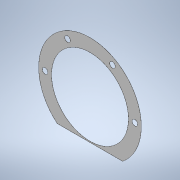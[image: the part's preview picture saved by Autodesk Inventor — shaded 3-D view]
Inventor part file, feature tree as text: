
AUTODESK INVENTOR PART (.ipt)
format: ipt  version: 2020 (Build 240168000, 168)  size: 114,176 bytes
history: native  units: mm
features: other x3, plane x1, extrude x1, sketch x1, reference x1
ambient origin geometry x8: Origin, YZ Plane, XZ Plane, XY Plane, X Axis, Y Axis, Z Axis, Center Point
bodies: 实体1 (feature_tree)
feature tree (7):
  plane  "工作平面1"
  extrude  "拉伸1"  [1 undecoded]
  sketch  "草图1"  dims[d0=0.18mm d1=0.0mm]
  reference  "参考1"
  other  "<userpath>\Desktop\ME_course_project\课设试试\shaft_try_1.iam"
  other  "shaft_try_1.iam"
  other  "轴承端盖3:1"
note: 1 required parameter value undecoded (feature->parameter linkage not recoverable at this tier; creation-order binding heuristic only, values carry confidence <= 0.55)
